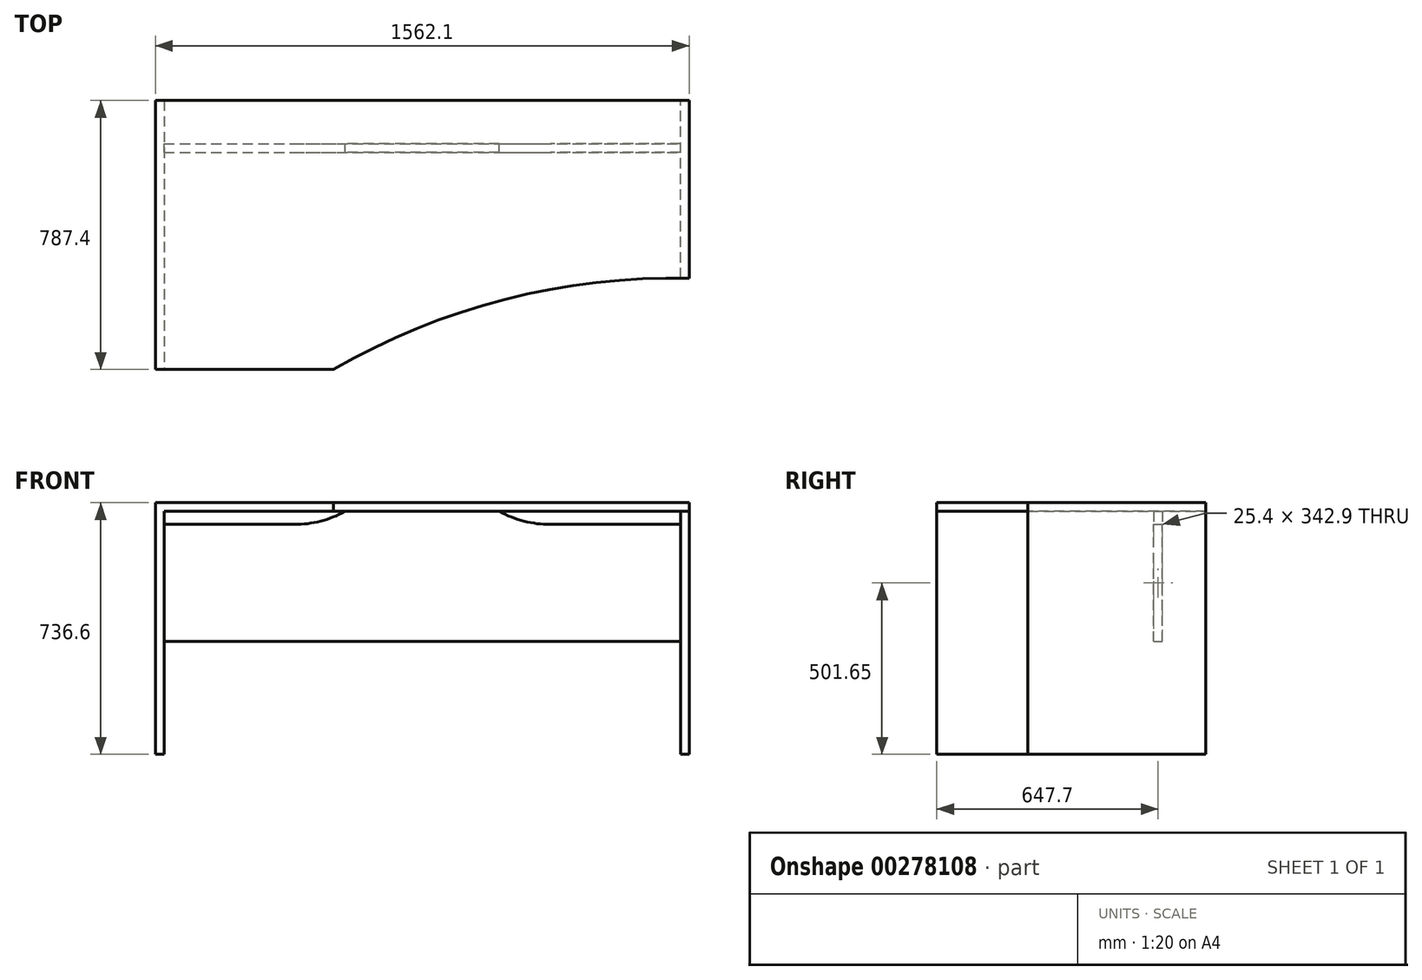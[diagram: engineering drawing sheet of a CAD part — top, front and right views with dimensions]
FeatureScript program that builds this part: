
annotation { "Feature Type Name" : "Feature", "Feature Type Description" : "" }
export const myFeature = defineFeature(function(context is Context, id is Id, definition is map)
    precondition{}
    {
        {
            var Q0;
            Q0=qCreatedBy(makeId("Top.planeOp"),FACE);
            var sketch = newSketch(context, id + "F0", { "sketchPlane" : qUnion([Q0])});
            skLineSegment(sketch, "E0.bottom", {"start": v(0, 0) * mm, "end": v(25.4, 0) * mm});
            skLineSegment(sketch, "E0.top", {"start": v(0, -787.4) * mm, "end": v(25.4, -787.4) * mm});
            skLineSegment(sketch, "E0.left", {"start": v(0, 0) * mm, "end": v(0, -787.4) * mm});
            skLineSegment(sketch, "E0.right", {"start": v(25.4, 0) * mm, "end": v(25.4, -787.4) * mm});
            skSolve(sketch);
        }
        {
            var Q0;
            Q0=makeQuery(id+"F0.imprint","IMPRINT",FACE,{"disambiguationData":[TD([[makeQuery(id+"F0.imprint","IMPRINT",EDGE,{"derivedFrom":sQuery(id+"F0.wireOp",EDGE,"E0.bottom")}),-1.0]])]});
            extrude(context, id + "F1", {"entities" : qUnion([Q0]), "depth" : 711.2 * mm});
        }
        {
            var Q0;
            Q0=makeQuery(id+"F1.opExtrude","CAP_FACE",FACE,{"disambiguationData":[OSD([sQuery(id+"F0.wireOp",EDGE,"E0.bottom"),sQuery(id+"F0.wireOp",EDGE,"E0.top"),sQuery(id+"F0.wireOp",EDGE,"E0.left"),sQuery(id+"F0.wireOp",EDGE,"E0.right")])],"isStart":false});
            var sketch = newSketch(context, id + "F2", { "sketchPlane" : qUnion([Q0])});
            skLineSegment(sketch, "E1.bottom", {"start": v(0, 0) * mm, "end": v(1562.1, 0) * mm});
            skLineSegment(sketch, "E1.top", {"start": v(0, -787.4) * mm, "end": v(1562.1, -787.4) * mm});
            skLineSegment(sketch, "E1.left", {"start": v(0, 0) * mm, "end": v(0, -787.4) * mm});
            skLineSegment(sketch, "E1.right", {"start": v(1562.1, 0) * mm, "end": v(1562.1, -787.4) * mm});
            skArc(sketch, "E2", {"start": v(1562.1, -520.7) * mm, "mid": v(1022.97, -582.07) * mm, "end": v(520.7, -787.4) * mm});
            skSolve(sketch);
        }
        {
            var Q0;
            {var subQ3=sQuery(id+"F2.wireOp",EDGE,"E2");Q0=makeQuery(id+"F2.imprint","IMPRINT",FACE,{"disambiguationData":[TD([[makeQuery(id+"F2.imprint","IMPRINT",EDGE,{"derivedFrom":subQ3}),-1.0]])]});}
            var Q1;
            {var subQ0=sQuery(id+"F2.wireOp",EDGE,"E1.left");Q1=makeQuery(id+"F2.imprint","IMPRINT",FACE,{"disambiguationData":[TD([[makeQuery(id+"F2.imprint","IMPRINT",EDGE,{"derivedFrom":subQ0}),1.0]])]});}
            extrude(context, id + "F3", {"entities" : qUnion([Q0, Q1]), "operationType" : NewBodyOperationType.ADD, "depth" : 25.4 * mm});
        }
        {
            var Q0;
            Q0=qCreatedBy(makeId("Top.planeOp"),FACE);
            var sketch = newSketch(context, id + "F4", { "sketchPlane" : qUnion([Q0])});
            skLineSegment(sketch, "E3.bottom", {"start": v(1562.1, -520.7) * mm, "end": v(1536.7, -520.7) * mm});
            skLineSegment(sketch, "E3.top", {"start": v(1562.1, 0) * mm, "end": v(1536.7, 0) * mm});
            skLineSegment(sketch, "E3.left", {"start": v(1562.1, -520.7) * mm, "end": v(1562.1, 0) * mm});
            skLineSegment(sketch, "E3.right", {"start": v(1536.7, -520.7) * mm, "end": v(1536.7, 0) * mm});
            skSolve(sketch);
        }
        {
            var Q0;
            Q0 = qSketchRegion(id + "F4", true);
            extrude(context, id + "F5", {"entities" : qUnion([Q0]), "operationType" : NewBodyOperationType.ADD, "depth" : 711.2 * mm});
        }
        {
            var Q0;
            Q0=qCreatedBy(makeId("Front.planeOp"),FACE);
            cPlane(context, id + "F6", {"entities" : qUnion([Q0]), "cplaneType" : CPlaneType.OFFSET, "offset" : 127 * mm, "width" : 152.4 * mm, "height" : 152.4 * mm});
        }
        {
            var Q0;
            Q0=qCreatedBy(id+"F6.planeOp",FACE);
            var sketch = newSketch(context, id + "F7", { "sketchPlane" : qUnion([Q0])});
            skLineSegment(sketch, "E4", {"start": v(25.4, 330.2) * mm, "end": v(1536.7, 330.2) * mm});
            skLineSegment(sketch, "E5", {"start": v(1536.7, 330.2) * mm, "end": v(1536.7, 673.1) * mm});
            skLineSegment(sketch, "E6", {"start": v(1536.7, 673.1) * mm, "end": v(1155.7, 673.1) * mm});
            skArc(sketch, "E7", {"start": v(1006.8, 711.2) * mm, "mid": v(1078.86, 682.78) * mm, "end": v(1155.7, 673.1) * mm});
            skLineSegment(sketch, "E8", {"start": v(1006.8, 711.2) * mm, "end": v(555.3, 711.2) * mm});
            skLineSegment(sketch, "E9", {"start": v(25.4, 330.2) * mm, "end": v(25.4, 673.1) * mm});
            skLineSegment(sketch, "E10", {"start": v(25.4, 673.1) * mm, "end": v(406.4, 673.1) * mm});
            skArc(sketch, "E11", {"start": v(406.4, 673.1) * mm, "mid": v(483.24, 682.78) * mm, "end": v(555.3, 711.2) * mm});
            skSolve(sketch);
        }
        {
            var Q0;
            Q0 = qSketchRegion(id + "F7", true);
            extrude(context, id + "F8", {"entities" : qUnion([Q0]), "operationType" : NewBodyOperationType.ADD, "depth" : 25.4 * mm});
        }
    });
